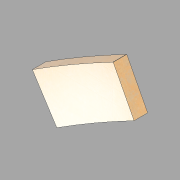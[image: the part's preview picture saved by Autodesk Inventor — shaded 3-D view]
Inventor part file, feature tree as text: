
AUTODESK INVENTOR PART (.ipt)
format: ipt  version: 2022.1 (Build 261234020, 234B)  size: 93,184 bytes
history: imported  units: in
note: dims shown in document units (in); Inventor stores cm internally (conversion verified against a paired STEP export)
features: imported_body x1
ambient origin geometry x8: Origin, YZ Plane, XZ Plane, XY Plane, X Axis, Y Axis, Z Axis, Center Point
bodies: Solid1 (imported_parasolid), Body1 (imported_parasolid)
feature tree (1):
  imported_body  NMx_Import_Brep_tag  [imported B-rep: ~7 faces, bbox_mm=[1140.79376, 952.251867, 152.4]]
